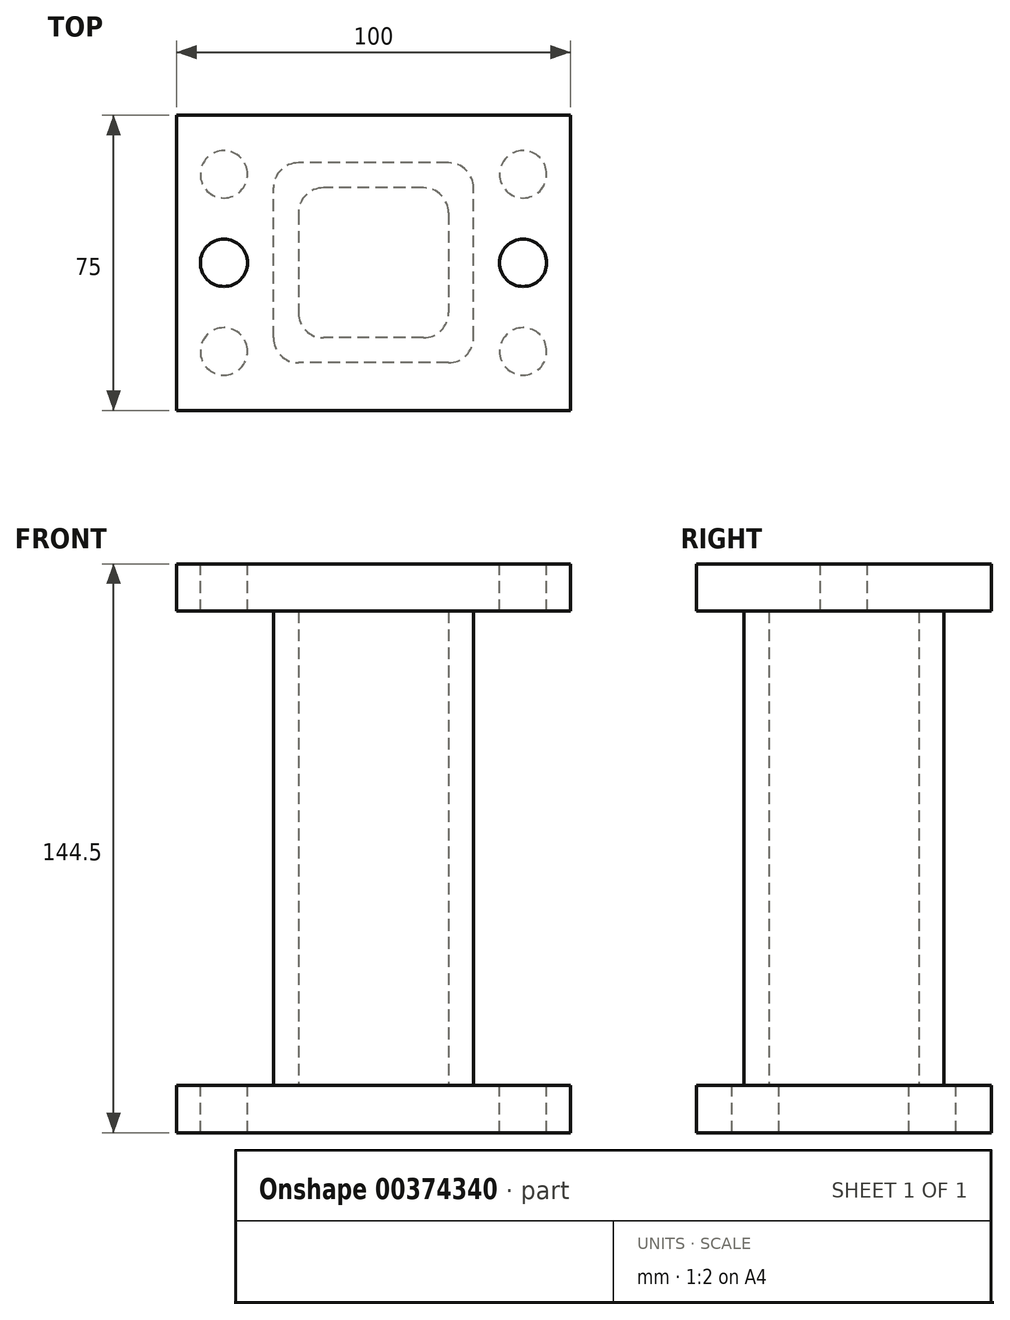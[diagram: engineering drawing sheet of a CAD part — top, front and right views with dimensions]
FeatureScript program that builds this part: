
annotation { "Feature Type Name" : "Feature", "Feature Type Description" : "" }
export const myFeature = defineFeature(function(context is Context, id is Id, definition is map)
    precondition{}
    {
        {
            var Q0;
            Q0=qCreatedBy(makeId("Top.planeOp"),FACE);
            var sketch = newSketch(context, id + "F0", { "sketchPlane" : qUnion([Q0])});
            skLineSegment(sketch, "E0.bottom", {"start": v(50, 37.5) * mm, "end": v(-50, 37.5) * mm});
            skLineSegment(sketch, "E0.top", {"start": v(50, -37.5) * mm, "end": v(-50, -37.5) * mm});
            skLineSegment(sketch, "E0.left", {"start": v(50, 37.5) * mm, "end": v(50, -37.5) * mm});
            skLineSegment(sketch, "E0.right", {"start": v(-50, 37.5) * mm, "end": v(-50, -37.5) * mm});
            skPoint(sketch, "E0.middle", {"position": v(0, 0) * mm});
            skSolve(sketch);
        }
        {
            var Q0;
            Q0=makeQuery(id+"F0.imprint","IMPRINT",FACE,{"disambiguationData":[TD([[makeQuery(id+"F0.imprint","IMPRINT",EDGE,{"derivedFrom":sQuery(id+"F0.wireOp",EDGE,"E0.bottom")}),1.0]])]});
            extrude(context, id + "F1", {"entities" : qUnion([Q0]), "depth" : -12 * mm});
        }
        {
            var Q0;
            Q0=makeQuery(id+"F1.opExtrude","CAP_FACE",FACE,{"disambiguationData":[OSD([sQuery(id+"F0.wireOp",EDGE,"E0.bottom"),sQuery(id+"F0.wireOp",EDGE,"E0.top"),sQuery(id+"F0.wireOp",EDGE,"E0.left"),sQuery(id+"F0.wireOp",EDGE,"E0.right")])],"isStart":true});
            var sketch = newSketch(context, id + "F2", { "sketchPlane" : qUnion([Q0])});
            skLineSegment(sketch, "E1.bottom", {"start": v(19.05, -25.4) * mm, "end": v(-19.05, -25.4) * mm});
            skLineSegment(sketch, "E1.top", {"start": v(19.05, 25.4) * mm, "end": v(-19.05, 25.4) * mm});
            skLineSegment(sketch, "E1.left", {"start": v(25.4, -19.05) * mm, "end": v(25.4, 19.05) * mm});
            skLineSegment(sketch, "E1.right", {"start": v(-25.4, -19.05) * mm, "end": v(-25.4, 19.05) * mm});
            skPoint(sketch, "E1.middle", {"position": v(0, 0) * mm});
            skPoint(sketch, "E2.visualSharp", {"position": v(-25.4, -25.4) * mm});
            skArc(sketch, "E2.filletArc", {"start": v(-25.4, -19.05) * mm, "mid": v(-23.54, -23.54) * mm, "end": v(-19.05, -25.4) * mm});
            skPoint(sketch, "E3.visualSharp", {"position": v(-25.4, 25.4) * mm});
            skArc(sketch, "E3.filletArc", {"start": v(-19.05, 25.4) * mm, "mid": v(-23.54, 23.54) * mm, "end": v(-25.4, 19.05) * mm});
            skPoint(sketch, "E4.visualSharp", {"position": v(25.4, 25.4) * mm});
            skArc(sketch, "E4.filletArc", {"start": v(25.4, 19.05) * mm, "mid": v(23.54, 23.54) * mm, "end": v(19.05, 25.4) * mm});
            skPoint(sketch, "E5.visualSharp", {"position": v(25.4, -25.4) * mm});
            skArc(sketch, "E5.filletArc", {"start": v(19.05, -25.4) * mm, "mid": v(23.54, -23.54) * mm, "end": v(25.4, -19.05) * mm});
            skLineSegment(sketch, "E6.bottom", {"start": v(12.7, 19.05) * mm, "end": v(-12.7, 19.05) * mm});
            skLineSegment(sketch, "E6.top", {"start": v(12.7, -19.05) * mm, "end": v(-12.7, -19.05) * mm});
            skLineSegment(sketch, "E6.left", {"start": v(19.05, 12.7) * mm, "end": v(19.05, -12.7) * mm});
            skLineSegment(sketch, "E6.right", {"start": v(-19.05, 12.7) * mm, "end": v(-19.05, -12.7) * mm});
            skArc(sketch, "E7.filletArc", {"start": v(-12.7, 19.05) * mm, "mid": v(-17.2, 17.2) * mm, "end": v(-19.05, 12.7) * mm});
            skArc(sketch, "E8.filletArc", {"start": v(19.05, 12.7) * mm, "mid": v(17.2, 17.2) * mm, "end": v(12.7, 19.05) * mm});
            skArc(sketch, "E9.filletArc", {"start": v(12.7, -19.05) * mm, "mid": v(17.2, -17.2) * mm, "end": v(19.05, -12.7) * mm});
            skArc(sketch, "E10.filletArc", {"start": v(-19.05, -12.7) * mm, "mid": v(-17.2, -17.2) * mm, "end": v(-12.7, -19.05) * mm});
            skSolve(sketch);
        }
        {
            var Q0;
            Q0 = qSketchRegion(id + "F2", true);
            extrude(context, id + "F3", {"entities" : qUnion([Q0]), "operationType" : NewBodyOperationType.ADD, "depth" : 120.5 * mm});
        }
        {
            var Q0;
            {var subQ0=sQuery(id+"F0.wireOp",EDGE,"E0.left");var subQ1=sQuery(id+"F0.wireOp",EDGE,"E0.bottom");var subQ2=sQuery(id+"F0.wireOp",EDGE,"E0.right");var subQ3=sQuery(id+"F0.wireOp",EDGE,"E0.top");Q0=makeQuery(id+"F3.boolean.opBoolean","SPLIT",FACE,{"disambiguationData":[TD([makeQuery(id+"F1.opExtrude","SWEPT_FACE",FACE,{"disambiguationData":[OSD([subQ1])]})])],"derivedFrom":makeQuery(id+"F1.opExtrude","CAP_FACE",FACE,{"disambiguationData":[OSD([subQ1,subQ3,subQ0,subQ2])],"isStart":true})});}
            var sketch = newSketch(context, id + "F4", { "sketchPlane" : qUnion([Q0])});
            skLineSegment(sketch, "E11", {"start": v(-50, -37.5) * mm, "end": v(-38, -37.5) * mm, "construction": true});
            skLineSegment(sketch, "E12", {"start": v(-38, -37.5) * mm, "end": v(-38, -22.5) * mm, "construction": true});
            skLineSegment(sketch, "E13", {"start": v(-50, 37.5) * mm, "end": v(-38, 37.5) * mm, "construction": true});
            skLineSegment(sketch, "E14", {"start": v(-38, 37.5) * mm, "end": v(-38, 22.5) * mm, "construction": true});
            skLineSegment(sketch, "E15", {"start": v(50, 37.5) * mm, "end": v(38, 37.5) * mm, "construction": true});
            skLineSegment(sketch, "E16", {"start": v(50, -37.5) * mm, "end": v(38, -37.5) * mm, "construction": true});
            skLineSegment(sketch, "E17", {"start": v(38, -37.5) * mm, "end": v(38, -22.5) * mm, "construction": true});
            skLineSegment(sketch, "E18", {"start": v(38, 37.5) * mm, "end": v(38, 22.5) * mm, "construction": true});
            skSolve(sketch);
        }
        {
            var Q0;
            Q0=makeQuery(id+"F3.opExtrude","CAP_FACE",FACE,{"disambiguationData":[OSD([sQuery(id+"F2.wireOp",EDGE,"E1.bottom"),sQuery(id+"F2.wireOp",EDGE,"E1.top"),sQuery(id+"F2.wireOp",EDGE,"E1.left"),sQuery(id+"F2.wireOp",EDGE,"E1.right"),sQuery(id+"F2.wireOp",EDGE,"E2.filletArc"),sQuery(id+"F2.wireOp",EDGE,"E3.filletArc"),sQuery(id+"F2.wireOp",EDGE,"E4.filletArc"),sQuery(id+"F2.wireOp",EDGE,"E5.filletArc"),sQuery(id+"F2.wireOp",EDGE,"E6.bottom"),sQuery(id+"F2.wireOp",EDGE,"E6.top"),sQuery(id+"F2.wireOp",EDGE,"E6.left"),sQuery(id+"F2.wireOp",EDGE,"E6.right"),sQuery(id+"F2.wireOp",EDGE,"E7.filletArc"),sQuery(id+"F2.wireOp",EDGE,"E8.filletArc"),sQuery(id+"F2.wireOp",EDGE,"E9.filletArc"),sQuery(id+"F2.wireOp",EDGE,"E10.filletArc")])],"isStart":false});
            var sketch = newSketch(context, id + "F5", { "sketchPlane" : qUnion([Q0])});
            skLineSegment(sketch, "E19.bottom", {"start": v(50, -37.5) * mm, "end": v(-50, -37.5) * mm});
            skLineSegment(sketch, "E19.top", {"start": v(50, 37.5) * mm, "end": v(-50, 37.5) * mm});
            skLineSegment(sketch, "E19.left", {"start": v(50, -37.5) * mm, "end": v(50, 37.5) * mm});
            skLineSegment(sketch, "E19.right", {"start": v(-50, -37.5) * mm, "end": v(-50, 37.5) * mm});
            skPoint(sketch, "E19.middle", {"position": v(0, 0) * mm});
            skSolve(sketch);
        }
        {
            var Q0;
            Q0=makeQuery(id+"F5.imprint","IMPRINT",FACE,{"disambiguationData":[TD([[makeQuery(id+"F5.imprint","IMPRINT",EDGE,{"derivedFrom":makeQuery(id+"F3.opExtrude","CAP_EDGE",EDGE,{"disambiguationData":[OSD([sQuery(id+"F2.wireOp",EDGE,"E6.bottom")])],"isStart":false})}),1.0]])]});
            var Q1;
            Q1=makeQuery(id+"F5.imprint","IMPRINT",FACE,{"disambiguationData":[TD([[makeQuery(id+"F5.imprint","IMPRINT",EDGE,{"derivedFrom":sQuery(id+"F5.wireOp",EDGE,"E19.bottom")}),-1.0]])]});
            var Q2;
            Q2=makeQuery(id+"F5.imprint","IMPRINT",FACE,{"disambiguationData":[TD([[makeQuery(id+"F5.imprint","IMPRINT",EDGE,{"derivedFrom":makeQuery(id+"F3.opExtrude","CAP_EDGE",EDGE,{"disambiguationData":[OSD([sQuery(id+"F2.wireOp",EDGE,"E1.bottom")])],"isStart":false})}),-1.0]])]});
            extrude(context, id + "F6", {"entities" : qUnion([Q0, Q1, Q2]), "operationType" : NewBodyOperationType.ADD, "depth" : 12 * mm});
        }
        {
            var Q0;
            Q0=makeQuery(id+"F6.opExtrude","CAP_FACE",FACE,{"disambiguationData":[OSD([sQuery(id+"F5.wireOp",EDGE,"E19.bottom"),sQuery(id+"F5.wireOp",EDGE,"E19.top"),sQuery(id+"F5.wireOp",EDGE,"E19.left"),sQuery(id+"F5.wireOp",EDGE,"E19.right")])],"isStart":false});
            var sketch = newSketch(context, id + "F7", { "sketchPlane" : qUnion([Q0])});
            skLineSegment(sketch, "E20", {"start": v(-50, 0) * mm, "end": v(-38, 0) * mm, "construction": true});
            skLineSegment(sketch, "E21", {"start": v(50, 0) * mm, "end": v(38, 0) * mm, "construction": true});
            skPoint(sketch, "E21.endSnap0", {"position": v(50, 0) * mm});
            skSolve(sketch);
        }
        {
            var Q0;
            Q0=sQuery(id+"F7.wireOp",VERTEX,"E20.end");
            var Q1;
            Q1=sQuery(id+"F7.wireOp",VERTEX,"E21.end");
            var Q2;
            Q2=makeQuery(id+"F1.opExtrude","SWEPT_BODY",BODY,{"disambiguationData":[OSD([sQuery(id+"F0.wireOp",EDGE,"E0.bottom"),sQuery(id+"F0.wireOp",EDGE,"E0.top"),sQuery(id+"F0.wireOp",EDGE,"E0.left"),sQuery(id+"F0.wireOp",EDGE,"E0.right")])]});
            hole(context, id + "F8", {"style" : HoleStyle.SIMPLE, "endStyle" : HoleEndStyle.BLIND, "holeDiameter" : 12 * mm, "holeDepth" : 12 * mm, "isTappedThrough" : true, "tappedDepth" : 12 * mm, "tapClearance" : 3, "locations" : qUnion([Q0, Q1]), "scope" : qUnion([Q2])});
        }
        {
            var Q0;
            Q0=sQuery(id+"F4.wireOp",VERTEX,"E14.end");
            var Q1;
            Q1=sQuery(id+"F4.wireOp",VERTEX,"E18.end");
            var Q2;
            Q2=sQuery(id+"F4.wireOp",VERTEX,"E17.end");
            var Q3;
            Q3=sQuery(id+"F4.wireOp",VERTEX,"E12.end");
            var Q4;
            Q4=makeQuery(id+"F1.opExtrude","SWEPT_BODY",BODY,{"disambiguationData":[OSD([sQuery(id+"F0.wireOp",EDGE,"E0.bottom"),sQuery(id+"F0.wireOp",EDGE,"E0.top"),sQuery(id+"F0.wireOp",EDGE,"E0.left"),sQuery(id+"F0.wireOp",EDGE,"E0.right")])]});
            hole(context, id + "F9", {"style" : HoleStyle.SIMPLE, "endStyle" : HoleEndStyle.BLIND, "holeDiameter" : 12 * mm, "holeDepth" : 12 * mm, "isTappedThrough" : true, "tappedDepth" : 12 * mm, "tapClearance" : 3, "locations" : qUnion([Q0, Q1, Q2, Q3]), "scope" : qUnion([Q4])});
        }
    });
